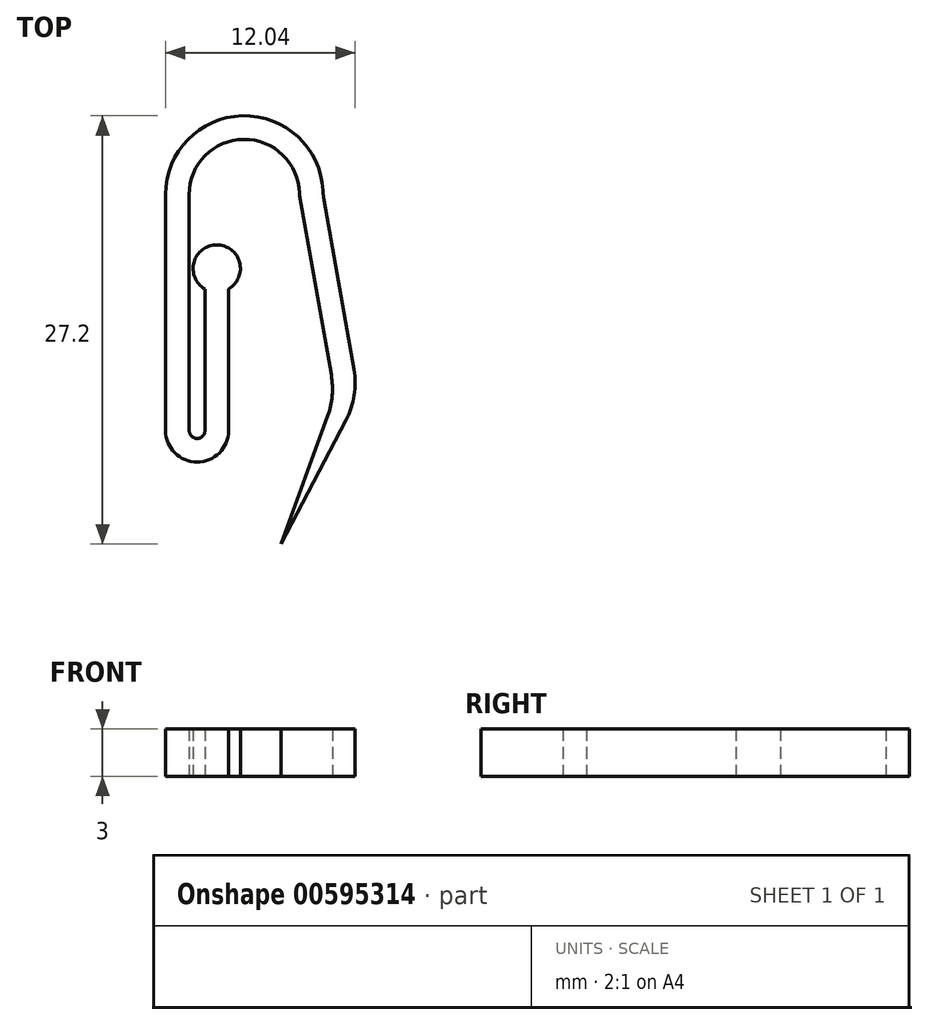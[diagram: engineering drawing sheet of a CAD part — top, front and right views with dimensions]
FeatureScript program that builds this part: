
annotation { "Feature Type Name" : "Feature", "Feature Type Description" : "" }
export const myFeature = defineFeature(function(context is Context, id is Id, definition is map)
    precondition{}
    {
        {
            var Q0;
            Q0=qCreatedBy(makeId("Top.planeOp"),FACE);
            var sketch = newSketch(context, id + "F0", { "sketchPlane" : qUnion([Q0])});
            skLineSegment(sketch, "E0", {"start": v(0, 0) * mm, "end": v(0, 15) * mm});
            skLineSegment(sketch, "E1", {"start": v(0, 0) * mm, "end": v(2, 0) * mm, "construction": true});
            skArc(sketch, "E2", {"start": v(2.5, 1.94) * mm, "mid": v(2, 2) * mm, "end": v(1.5, 1.94) * mm, "construction": true});
            skArc(sketch, "E3", {"start": v(1.5, 0) * mm, "mid": v(2, -0.5) * mm, "end": v(2.5, 0) * mm});
            skLineSegment(sketch, "E4", {"start": v(2.5, 0) * mm, "end": v(2.5, 9) * mm});
            skLineSegment(sketch, "E5", {"start": v(4, 0) * mm, "end": v(4, 9) * mm});
            skCircle(sketch, "E6", {"center": v(2.5, 9) * mm, "radius": 1.5 * mm, "construction": true});
            skCircle(sketch, "E7", {"center": v(4, 9) * mm, "radius": 1.5 * mm, "construction": true});
            skArc(sketch, "E8", {"start": v(4, 9) * mm, "mid": v(3.25, 11.8) * mm, "end": v(2.5, 9) * mm});
            skLineSegment(sketch, "E9", {"start": v(1.5, 0) * mm, "end": v(1.5, 15) * mm});
            skLineSegment(sketch, "E10", {"start": v(0, 15) * mm, "end": v(5, 15) * mm, "construction": true});
            skArc(sketch, "E11", {"start": v(10, 15.26) * mm, "mid": v(4.87, 20) * mm, "end": v(0, 15) * mm});
            skArc(sketch, "E12", {"start": v(8.5, 15.07) * mm, "mid": v(4.96, 18.5) * mm, "end": v(1.5, 15) * mm});
            skLineSegment(sketch, "E13", {"start": v(8.51, 14.92) * mm, "end": v(10.52, 3.52) * mm});
            skLineSegment(sketch, "E14", {"start": v(10.06, 14.64) * mm, "end": v(11.96, 3.88) * mm});
            skLineSegment(sketch, "E15", {"start": v(10.3, 0.94) * mm, "end": v(7.34, -7.2) * mm});
            skLineSegment(sketch, "E16", {"start": v(11.47, 0.69) * mm, "end": v(7.34, -7.2) * mm});
            skArc(sketch, "E17.trimOffspring", {"start": v(0, 0) * mm, "mid": v(2, -2) * mm, "end": v(4, 0) * mm});
            skPoint(sketch, "E18.visualSharp", {"position": v(12.26, 2.2) * mm});
            skArc(sketch, "E18.filletArc", {"start": v(11.47, 0.69) * mm, "mid": v(11.98, 2.24) * mm, "end": v(11.96, 3.88) * mm});
            skPoint(sketch, "E19.visualSharp", {"position": v(10.76, 2.2) * mm});
            skArc(sketch, "E19.filletArc", {"start": v(10.3, 0.94) * mm, "mid": v(10.58, 2.21) * mm, "end": v(10.52, 3.52) * mm});
            skPoint(sketch, "E20.visualSharp", {"position": v(8.5, 15) * mm});
            skArc(sketch, "E20.filletArc", {"start": v(8.5, 15.07) * mm, "mid": v(8.5, 15) * mm, "end": v(8.51, 14.92) * mm});
            skPoint(sketch, "E21.visualSharp", {"position": v(10, 15) * mm});
            skArc(sketch, "E21.filletArc", {"start": v(10, 15.26) * mm, "mid": v(10.02, 14.95) * mm, "end": v(10.06, 14.64) * mm});
            skSolve(sketch);
        }
        {
            var Q0;
            Q0 = qSketchRegion(id + "F0", true);
            var Q1;
            Q1=makeQuery(id+"F0.imprint","IMPRINT",FACE,{"disambiguationData":[TD([[makeQuery(id+"F0.imprint","IMPRINT",EDGE,{"derivedFrom":sQuery(id+"F0.wireOp",EDGE,"E0")}),-1.0]])]});
            extrude(context, id + "F1", {"entities" : qUnion([Q0, Q1]), "depth" : 3 * mm, "offsetDistance" : 25 * mm});
        }
    });
